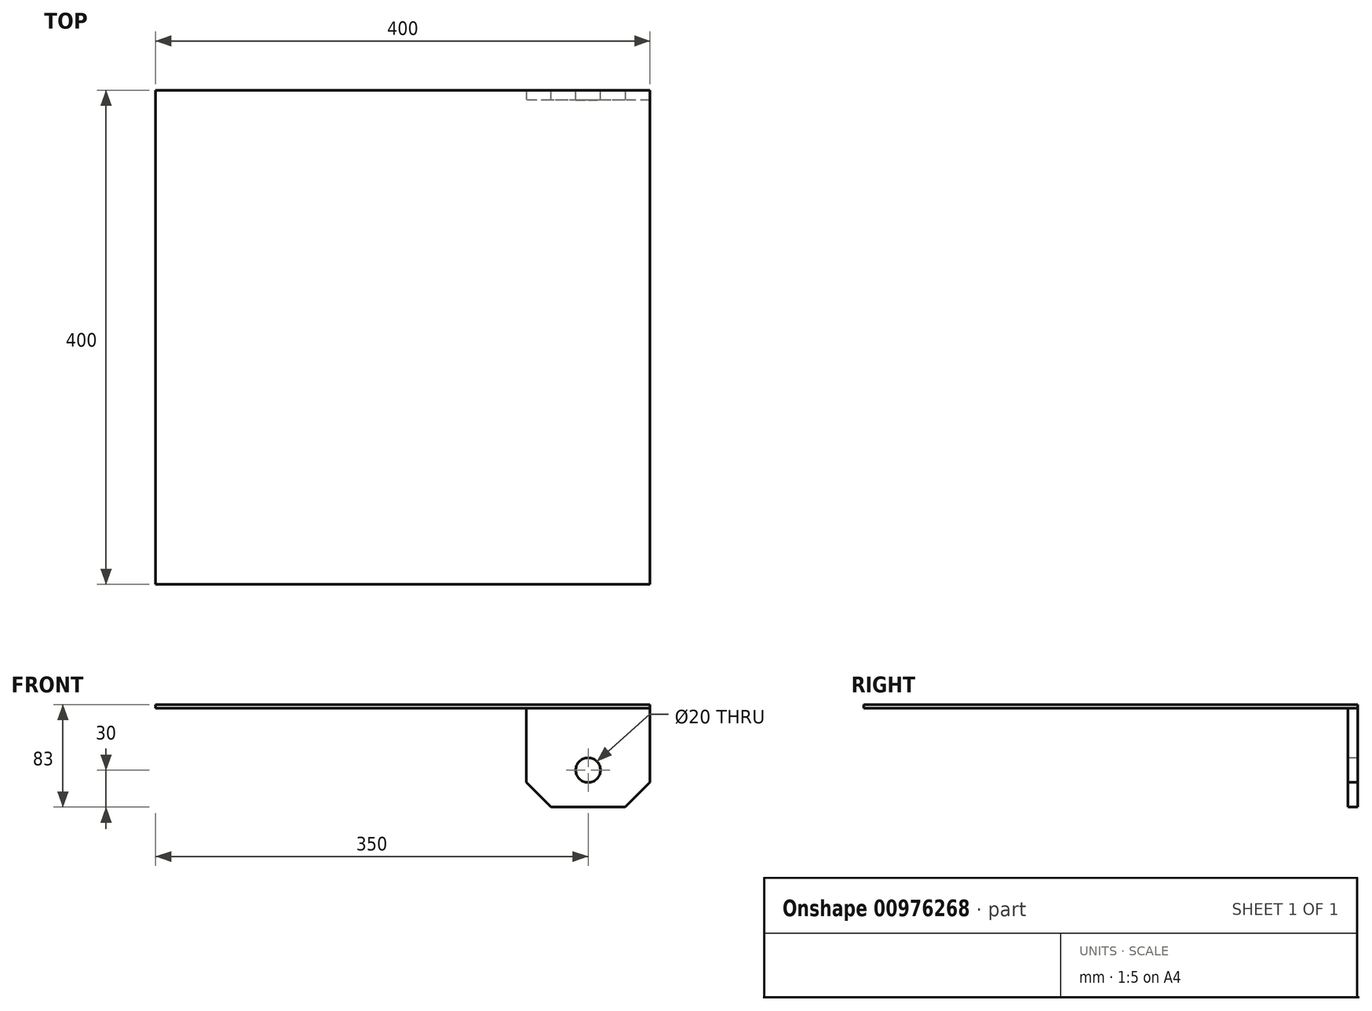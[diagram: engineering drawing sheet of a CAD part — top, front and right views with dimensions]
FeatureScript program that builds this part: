
annotation { "Feature Type Name" : "Feature", "Feature Type Description" : "" }
export const myFeature = defineFeature(function(context is Context, id is Id, definition is map)
    precondition{}
    {
        {
            var Q0;
            Q0=qCreatedBy(makeId("Top.planeOp"),FACE);
            var sketch = newSketch(context, id + "F0", { "sketchPlane" : qUnion([Q0])});
            skLineSegment(sketch, "E0.bottom", {"start": v(200, -200) * mm, "end": v(-200, -200) * mm});
            skLineSegment(sketch, "E0.top", {"start": v(200, 200) * mm, "end": v(-200, 200) * mm});
            skLineSegment(sketch, "E0.left", {"start": v(200, -200) * mm, "end": v(200, 200) * mm});
            skLineSegment(sketch, "E0.right", {"start": v(-200, -200) * mm, "end": v(-200, 200) * mm});
            skPoint(sketch, "E0.middle", {"position": v(0, 0) * mm});
            skSolve(sketch);
        }
        {
            var Q0;
            Q0=makeQuery(id+"F0.imprint","IMPRINT",FACE,{"disambiguationData":[TD([[makeQuery(id+"F0.imprint","IMPRINT",EDGE,{"derivedFrom":sQuery(id+"F0.wireOp",EDGE,"E0.bottom")}),-1.0]])]});
            extrude(context, id + "F1", {"entities" : qUnion([Q0]), "depth" : 3 * mm, "offsetDistance" : 25 * mm});
        }
        {
            var Q0;
            Q0=makeQuery(id+"F1.opExtrude","CAP_FACE",FACE,{"disambiguationData":[OSD([sQuery(id+"F0.wireOp",EDGE,"E0.bottom"),sQuery(id+"F0.wireOp",EDGE,"E0.top"),sQuery(id+"F0.wireOp",EDGE,"E0.left"),sQuery(id+"F0.wireOp",EDGE,"E0.right")])],"isStart":true});
            var sketch = newSketch(context, id + "F2", { "sketchPlane" : qUnion([Q0])});
            skLineSegment(sketch, "E1.bottom", {"start": v(200, -200) * mm, "end": v(100, -200) * mm});
            skLineSegment(sketch, "E1.top", {"start": v(200, -192) * mm, "end": v(100, -192) * mm});
            skLineSegment(sketch, "E1.left", {"start": v(200, -200) * mm, "end": v(200, -192) * mm});
            skLineSegment(sketch, "E1.right", {"start": v(100, -200) * mm, "end": v(100, -192) * mm});
            skSolve(sketch);
        }
        {
            var Q0;
            Q0=makeQuery(id+"F2.imprint","IMPRINT",FACE,{"disambiguationData":[TD([[makeQuery(id+"F2.imprint","IMPRINT",EDGE,{"derivedFrom":sQuery(id+"F2.wireOp",EDGE,"E1.bottom")}),-1.0]])]});
            extrude(context, id + "F3", {"entities" : qUnion([Q0]), "depth" : 80 * mm, "offsetDistance" : 25 * mm});
        }
        {
            var Q0;
            Q0=makeQuery(id+"F3.opExtrude","CAP_EDGE",EDGE,{"disambiguationData":[OSD([sQuery(id+"F2.wireOp",EDGE,"E1.left")])],"isStart":false});
            chamfer(context, id + "F4", {"entities" : qUnion([Q0]), "width" : 20 * mm, "tangentPropagation" : true});
        }
        {
            var Q0;
            Q0=makeQuery(id+"F3.opExtrude","SWEPT_FACE",FACE,{"disambiguationData":[OSD([sQuery(id+"F2.wireOp",EDGE,"E1.bottom")])]});
            var sketch = newSketch(context, id + "F5", { "sketchPlane" : qUnion([Q0])});
            skCircle(sketch, "E2", {"center": v(-150, -50) * mm, "radius": 10 * mm});
            skSolve(sketch);
        }
        {
            var Q0;
            Q0=makeQuery(id+"F5.imprint","IMPRINT",FACE,{"disambiguationData":[TD([[makeQuery(id+"F5.imprint","IMPRINT",EDGE,{"derivedFrom":sQuery(id+"F5.wireOp",EDGE,"E2")}),1.0]])]});
            extrude(context, id + "F6", {"entities" : qUnion([Q0]), "operationType" : NewBodyOperationType.REMOVE, "oppositeDirection" : true, "depth" : 25 * mm, "offsetDistance" : 25 * mm});
        }
        {
            var Q0;
            Q0=makeQuery(id+"F3.opExtrude","CAP_EDGE",EDGE,{"disambiguationData":[OSD([sQuery(id+"F2.wireOp",EDGE,"E1.right")])],"isStart":false});
            chamfer(context, id + "F7", {"entities" : qUnion([Q0]), "width" : 20 * mm, "tangentPropagation" : true});
        }
    });
